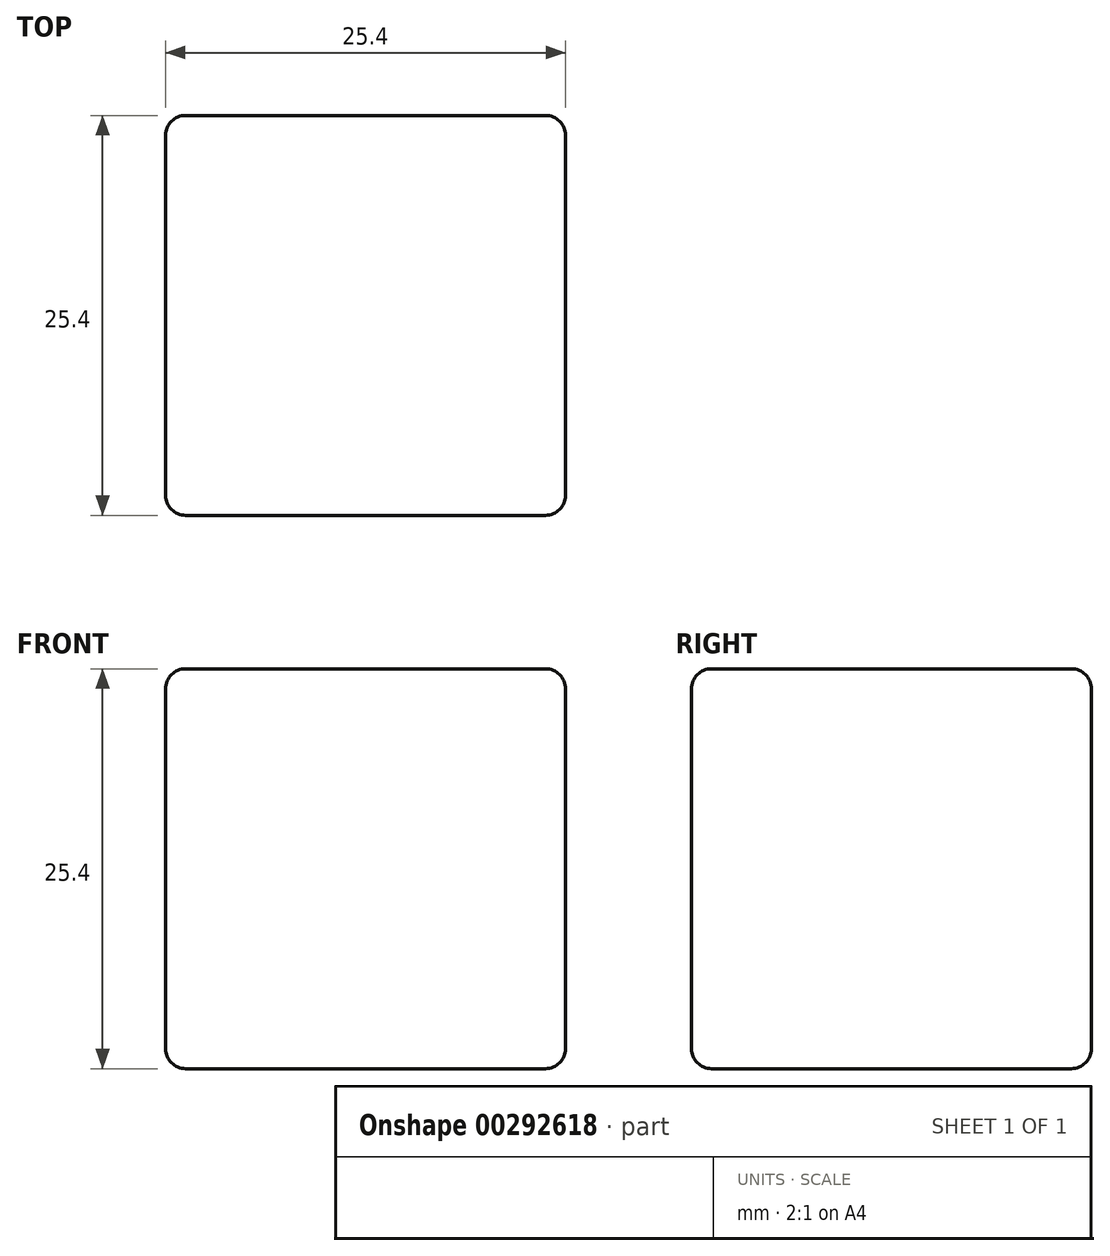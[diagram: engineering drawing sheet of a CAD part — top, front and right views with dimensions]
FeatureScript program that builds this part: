
annotation { "Feature Type Name" : "Feature", "Feature Type Description" : "" }
export const myFeature = defineFeature(function(context is Context, id is Id, definition is map)
    precondition{}
    {
        {
            var Q0;
            Q0=qCreatedBy(makeId("Top.planeOp"),FACE);
            var sketch = newSketch(context, id + "F0", { "sketchPlane" : qUnion([Q0])});
            skLineSegment(sketch, "E0.bottom", {"start": v(0, 0) * mm, "end": v(25.4, 0) * mm});
            skLineSegment(sketch, "E0.top", {"start": v(0, 25.4) * mm, "end": v(25.4, 25.4) * mm});
            skLineSegment(sketch, "E0.left", {"start": v(0, 0) * mm, "end": v(0, 25.4) * mm});
            skLineSegment(sketch, "E0.right", {"start": v(25.4, 0) * mm, "end": v(25.4, 25.4) * mm});
            skSolve(sketch);
        }
        {
            var Q0;
            Q0 = qSketchRegion(id + "F0", true);
            extrude(context, id + "F1", {"entities" : qUnion([Q0]), "depth" : 25.4 * mm});
        }
        {
            var Q0;
            Q0=makeQuery(id+"F1.opExtrude","CAP_EDGE",EDGE,{"disambiguationData":[OSD([sQuery(id+"F0.wireOp",EDGE,"E0.right")])],"isStart":false});
            var Q1;
            Q1=makeQuery(id+"F1.opExtrude","CAP_EDGE",EDGE,{"disambiguationData":[OSD([sQuery(id+"F0.wireOp",EDGE,"E0.bottom")])],"isStart":false});
            var Q2;
            Q2=makeQuery(id+"F1.opExtrude","CAP_EDGE",EDGE,{"disambiguationData":[OSD([sQuery(id+"F0.wireOp",EDGE,"E0.left")])],"isStart":false});
            var Q3;
            Q3=makeQuery(id+"F1.opExtrude","CAP_EDGE",EDGE,{"disambiguationData":[OSD([sQuery(id+"F0.wireOp",EDGE,"E0.top")])],"isStart":false});
            var Q4;
            Q4=makeQuery(id+"F1.opExtrude","CAP_EDGE",EDGE,{"disambiguationData":[OSD([sQuery(id+"F0.wireOp",EDGE,"E0.right")])],"isStart":true});
            var Q5;
            Q5=makeQuery(id+"F1.opExtrude","CAP_EDGE",EDGE,{"disambiguationData":[OSD([sQuery(id+"F0.wireOp",EDGE,"E0.bottom")])],"isStart":true});
            var Q6;
            Q6=makeQuery(id+"F1.opExtrude","SWEPT_FACE",FACE,{"disambiguationData":[OSD([sQuery(id+"F0.wireOp",EDGE,"E0.bottom")])]});
            var Q7;
            Q7=makeQuery(id+"F1.opExtrude","SWEPT_EDGE",EDGE,{"disambiguationData":[OSD([sQuery(id+"F0.wireOp",EDGE,"E0.top"),sQuery(id+"F0.wireOp",EDGE,"E0.right")])]});
            var Q8;
            Q8=makeQuery(id+"F1.opExtrude","CAP_EDGE",EDGE,{"disambiguationData":[OSD([sQuery(id+"F0.wireOp",EDGE,"E0.left")])],"isStart":true});
            var Q9;
            Q9=makeQuery(id+"F1.opExtrude","CAP_EDGE",EDGE,{"disambiguationData":[OSD([sQuery(id+"F0.wireOp",EDGE,"E0.top")])],"isStart":true});
            var Q10;
            Q10=makeQuery(id+"F1.opExtrude","SWEPT_EDGE",EDGE,{"disambiguationData":[OSD([sQuery(id+"F0.wireOp",EDGE,"E0.top"),sQuery(id+"F0.wireOp",EDGE,"E0.left")])]});
            fillet(context, id + "F2", {"entities" : qUnion([Q0, Q1, Q2, Q3, Q4, Q5, Q6, Q7, Q8, Q9, Q10]), "radius" : 1.27 * mm, "tangentPropagation" : true, "allowEdgeOverflow" : false});
        }
    });
